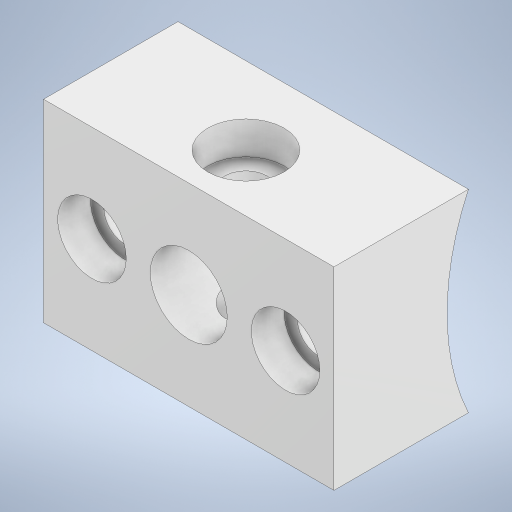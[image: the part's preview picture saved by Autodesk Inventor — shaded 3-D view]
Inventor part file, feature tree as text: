
AUTODESK INVENTOR PART (.ipt)
format: ipt  version: 2023 (Build 270158030, 158C)  size: 262,656 bytes
history: native  units: in
note: dims shown in document units (in); Inventor stores cm internally (conversion verified against a paired STEP export)
features: sketch x4, extrude x2, hole x2
ambient origin geometry x8: Origin, YZ Plane, XZ Plane, XY Plane, X Axis, Y Axis, Z Axis, Center Point
bodies: Solid1 (feature_tree)
feature tree (8):
  extrude  "Extrusion1"  Depth=1.5in TaperAngle=0.0deg
  extrude  "Extrusion6"  Depth=1.0in
  hole  "Hole2"  [1 undecoded]
  hole  "Hole3"  [1 undecoded]
  sketch  "Sketch1"  dims[d0=2.375in d4=1.5in d5=0.0in]
  sketch  "Sketch8"  dims[d47=1.7717in d48=1.0in]
  sketch  "Sketch10"  dims[d49=0.3976in d50=0.0in d51=0.0in]
  sketch  "Sketch11"  dims[d52=0.2165in d53=0.2362in d54=0.3937in d55=0.1693in d56=0.5635in d57=0.315in d58=0.8108in d60=0.2953in d61=0.2165in d62=0.2362in d63=0.3543in d64=0.1693in d65=90.0deg d66=0.315in d67=0.8108in d68=1.0in d69=0.0394in d70=0.0394in d71=0.0394in d72=0.0059in d73=0.2165in d74=0.0148in d75=0.5635in d76=0.0295in d77=0.8108in d78=0.0025in d79=0.0295in d80=0.0148in]
note: 2 required parameter values undecoded (feature->parameter linkage not recoverable at this tier; creation-order binding heuristic only, values carry confidence <= 0.55)
